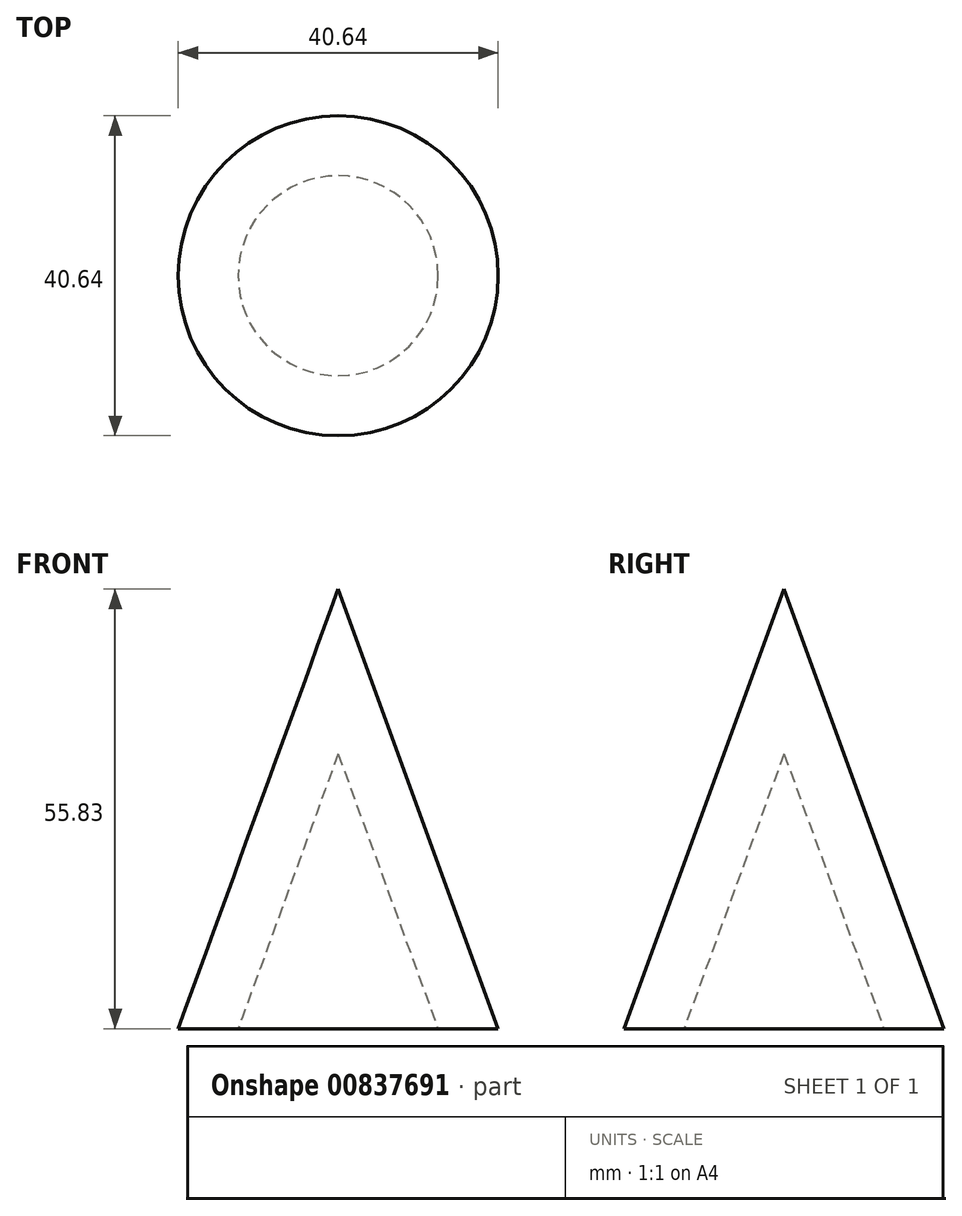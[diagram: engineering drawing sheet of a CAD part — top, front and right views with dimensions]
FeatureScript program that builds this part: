
annotation { "Feature Type Name" : "Feature", "Feature Type Description" : "" }
export const myFeature = defineFeature(function(context is Context, id is Id, definition is map)
    precondition{}
    {
        {
            var Q0;
            Q0=qCreatedBy(makeId("Front.planeOp"),FACE);
            var sketch = newSketch(context, id + "F0", { "sketchPlane" : qUnion([Q0])});
            skLineSegment(sketch, "E0", {"start": v(0, 39.16) * mm, "end": v(0, -46.66) * mm});
            skLineSegment(sketch, "E1", {"start": v(0, 55.83) * mm, "end": v(20.32, 0) * mm});
            skLineSegment(sketch, "E2", {"start": v(20.32, 0) * mm, "end": v(0, 0) * mm});
            skLineSegment(sketch, "E3", {"start": v(0, 0) * mm, "end": v(0, 55.83) * mm});
            skSolve(sketch);
        }
        {
            var Q0;
            Q0 = qSketchRegion(id + "F0", true);
            var Q1;
            Q1=sQuery(id+"F0.wireOp",EDGE,"E0");
            revolve(context, id + "F1", {"surfaceOperationType" : NewSurfaceOperationType.NEW, "entities" : qUnion([Q0]), "axis" : qUnion([Q1]), "revolveType" : RevolveType.FULL});
        }
        {
            var Q0;
            Q0=qCreatedBy(makeId("Front.planeOp"),FACE);
            var sketch = newSketch(context, id + "F2", { "sketchPlane" : qUnion([Q0])});
            skLineSegment(sketch, "E4", {"start": v(0, 24.01) * mm, "end": v(0, -22.1) * mm});
            skLineSegment(sketch, "E5", {"start": v(0, 34.9) * mm, "end": v(0, 0) * mm});
            skLineSegment(sketch, "E6", {"start": v(0, 0) * mm, "end": v(12.7, 0) * mm});
            skLineSegment(sketch, "E7", {"start": v(12.7, 0) * mm, "end": v(0, 34.9) * mm});
            skSolve(sketch);
        }
        {
            var Q0;
            Q0 = qSketchRegion(id + "F2", true);
            var Q1;
            Q1=sQuery(id+"F2.wireOp",EDGE,"E4");
            revolve(context, id + "F3", {"operationType" : NewBodyOperationType.REMOVE, "surfaceOperationType" : NewSurfaceOperationType.NEW, "entities" : qUnion([Q0]), "axis" : qUnion([Q1]), "revolveType" : RevolveType.FULL, "oppositeDirection" : true});
        }
    });
